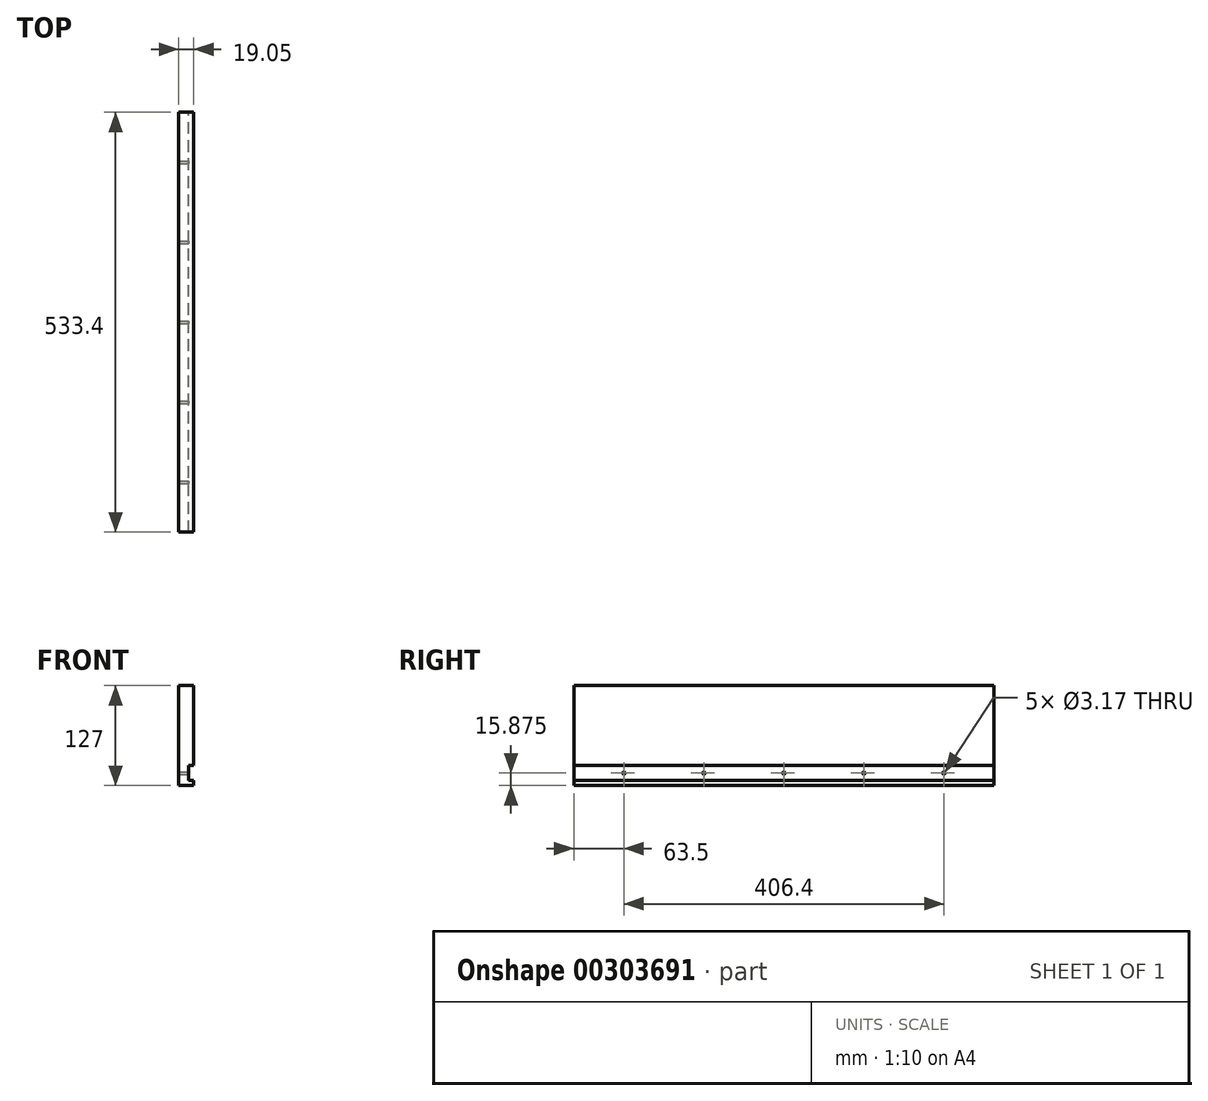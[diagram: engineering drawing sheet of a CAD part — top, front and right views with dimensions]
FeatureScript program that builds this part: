
annotation { "Feature Type Name" : "Feature", "Feature Type Description" : "" }
export const myFeature = defineFeature(function(context is Context, id is Id, definition is map)
    precondition{}
    {
        {
            var Q0;
            Q0=qCreatedBy(makeId("Right.planeOp"),FACE);
            var sketch = newSketch(context, id + "F0", { "sketchPlane" : qUnion([Q0])});
            skLineSegment(sketch, "E0.bottom", {"start": v(0, 0) * mm, "end": v(533.4, 0) * mm});
            skLineSegment(sketch, "E0.top", {"start": v(0, -127) * mm, "end": v(533.4, -127) * mm});
            skLineSegment(sketch, "E0.left", {"start": v(0, 0) * mm, "end": v(0, -127) * mm});
            skLineSegment(sketch, "E0.right", {"start": v(533.4, 0) * mm, "end": v(533.4, -127) * mm});
            skSolve(sketch);
        }
        {
            var Q0;
            Q0 = qSketchRegion(id + "F0", true);
            extrude(context, id + "F1", {"entities" : qUnion([Q0]), "oppositeDirection" : true, "depth" : 19.05 * mm});
        }
        {
            var Q0;
            Q0=qCreatedBy(makeId("Right.planeOp"),FACE);
            var sketch = newSketch(context, id + "F2", { "sketchPlane" : qUnion([Q0])});
            skLineSegment(sketch, "E1.bottom", {"start": v(0, -101.6) * mm, "end": v(533.4, -101.6) * mm});
            skLineSegment(sketch, "E1.top", {"start": v(0, -120.65) * mm, "end": v(533.4, -120.65) * mm});
            skLineSegment(sketch, "E1.left", {"start": v(0, -101.6) * mm, "end": v(0, -120.65) * mm});
            skLineSegment(sketch, "E1.right", {"start": v(533.4, -101.6) * mm, "end": v(533.4, -120.65) * mm});
            skSolve(sketch);
        }
        {
            var Q0;
            Q0 = qSketchRegion(id + "F2", true);
            extrude(context, id + "F3", {"entities" : qUnion([Q0]), "operationType" : NewBodyOperationType.REMOVE, "oppositeDirection" : true, "depth" : 6.35 * mm});
        }
        {
            var Q0;
            Q0=qCreatedBy(makeId("Right.planeOp"),FACE);
            var sketch = newSketch(context, id + "F4", { "sketchPlane" : qUnion([Q0])});
            skCircle(sketch, "E2", {"center": v(63.5, -111.12) * mm, "radius": 1.59 * mm});
            skCircle(sketch, "E3.1.0.0", {"center": v(165.1, -111.12) * mm, "radius": 1.59 * mm});
            skCircle(sketch, "E3.2.0.0", {"center": v(266.7, -111.12) * mm, "radius": 1.59 * mm});
            skCircle(sketch, "E3.3.0.0", {"center": v(368.3, -111.12) * mm, "radius": 1.59 * mm});
            skCircle(sketch, "E3.4.0.0", {"center": v(469.9, -111.12) * mm, "radius": 1.59 * mm});
            skLineSegment(sketch, "E3.direction1", {"start": v(63.5, -111.12) * mm, "end": v(165.1, -111.12) * mm, "construction": true});
            skSolve(sketch);
        }
        {
            var Q0;
            Q0 = qSketchRegion(id + "F4", true);
            extrude(context, id + "F5", {"entities" : qUnion([Q0]), "operationType" : NewBodyOperationType.REMOVE, "endBound" : BoundingType.THROUGH_ALL, "oppositeDirection" : true, "depth" : 25.4 * mm});
        }
    });
